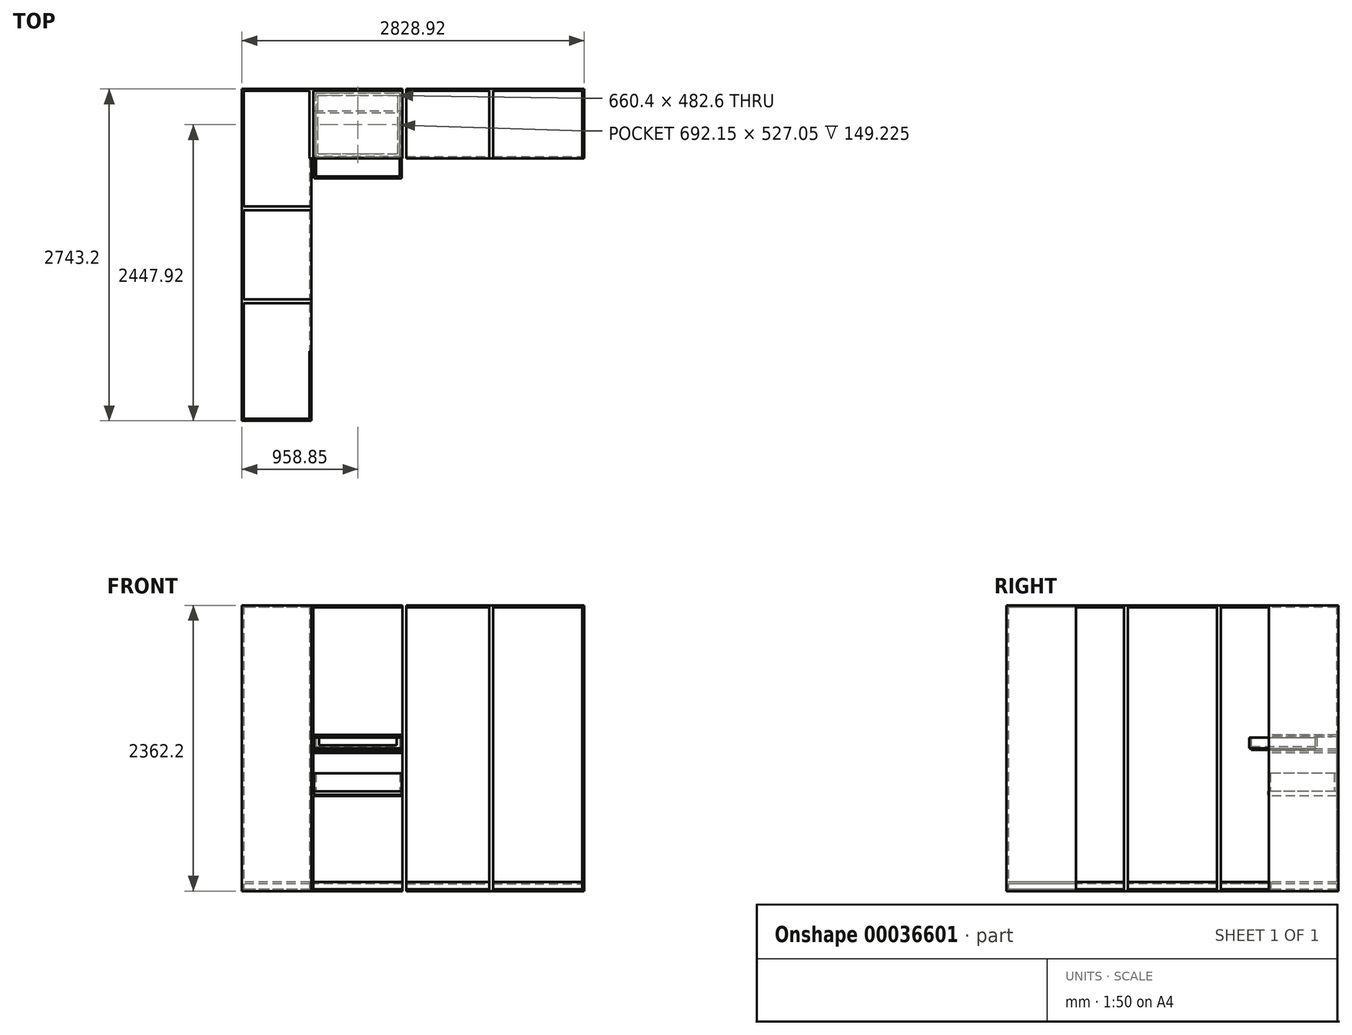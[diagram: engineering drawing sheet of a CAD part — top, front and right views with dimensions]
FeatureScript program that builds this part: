
annotation { "Feature Type Name" : "Feature", "Feature Type Description" : "" }
export const myFeature = defineFeature(function(context is Context, id is Id, definition is map)
    precondition{}
    {
        {
            var Q0;
            Q0=qCreatedBy(makeId("Top.planeOp"),FACE);
            var sketch = newSketch(context, id + "F0", { "sketchPlane" : qUnion([Q0])});
            skLineSegment(sketch, "E0.rect.bottom", {"start": v(384.18, 287.34) * mm, "end": v(-384.18, 287.34) * mm});
            skLineSegment(sketch, "E0.rect.top", {"start": v(384.18, -287.34) * mm, "end": v(-384.18, -287.34) * mm});
            skLineSegment(sketch, "E0.rect.left", {"start": v(384.18, 287.34) * mm, "end": v(384.18, -287.34) * mm});
            skLineSegment(sketch, "E0.rect.right", {"start": v(-384.18, 287.34) * mm, "end": v(-384.18, -287.34) * mm});
            skPoint(sketch, "E0.rect.middle", {"position": v(0, 0) * mm});
            skLineSegment(sketch, "E1.bottom", {"start": v(384.18, -287.34) * mm, "end": v(1101.73, -287.34) * mm});
            skLineSegment(sketch, "E1.top", {"start": v(384.17, 287.34) * mm, "end": v(1101.73, 287.34) * mm});
            skLineSegment(sketch, "E1.left", {"start": v(384.18, -287.34) * mm, "end": v(384.18, 287.34) * mm});
            skLineSegment(sketch, "E1.right", {"start": v(1101.73, -287.34) * mm, "end": v(1101.73, 287.34) * mm});
            skLineSegment(sketch, "E2.bottom", {"start": v(1101.73, -287.34) * mm, "end": v(1870.08, -287.34) * mm});
            skLineSegment(sketch, "E2.top", {"start": v(1101.73, 287.34) * mm, "end": v(1870.08, 287.34) * mm});
            skLineSegment(sketch, "E2.right", {"start": v(1870.08, -287.34) * mm, "end": v(1870.08, 287.34) * mm});
            skLineSegment(sketch, "E3.bottom", {"start": v(-384.18, 287.34) * mm, "end": v(-958.85, 287.34) * mm});
            skLineSegment(sketch, "E3.top", {"start": v(-384.17, -2455.86) * mm, "end": v(-958.85, -2455.86) * mm});
            skLineSegment(sketch, "E3.left", {"start": v(-384.18, 287.34) * mm, "end": v(-384.18, -2455.86) * mm});
            skLineSegment(sketch, "E3.right", {"start": v(-958.85, 287.34) * mm, "end": v(-958.85, -2455.86) * mm});
            skLineSegment(sketch, "E4.bottom", {"start": v(-384.17, -2455.86) * mm, "end": v(384.18, -2455.86) * mm});
            skLineSegment(sketch, "E4.top", {"start": v(-384.17, -1881.19) * mm, "end": v(384.18, -1881.19) * mm});
            skLineSegment(sketch, "E4.left", {"start": v(-384.17, -2455.86) * mm, "end": v(-384.17, -1881.19) * mm});
            skLineSegment(sketch, "E4.right", {"start": v(384.18, -2455.86) * mm, "end": v(384.18, -1881.19) * mm});
            skLineSegment(sketch, "E5.bottom", {"start": v(384.18, -2455.86) * mm, "end": v(1101.73, -2455.86) * mm});
            skLineSegment(sketch, "E5.top", {"start": v(384.18, -1881.19) * mm, "end": v(1101.73, -1881.19) * mm});
            skLineSegment(sketch, "E5.right", {"start": v(1101.73, -2455.86) * mm, "end": v(1101.73, -1881.19) * mm});
            skLineSegment(sketch, "E6.bottom", {"start": v(1101.73, -2455.86) * mm, "end": v(1870.08, -2455.86) * mm});
            skLineSegment(sketch, "E6.top", {"start": v(1101.73, -1881.19) * mm, "end": v(1870.08, -1881.19) * mm});
            skLineSegment(sketch, "E6.right", {"start": v(1870.08, -2455.86) * mm, "end": v(1870.08, -1881.19) * mm});
            skLineSegment(sketch, "E7.0", {"start": v(1117.6, -271.46) * mm, "end": v(1117.6, 271.46) * mm});
            skLineSegment(sketch, "E7.1", {"start": v(1117.6, -271.46) * mm, "end": v(1854.2, -271.46) * mm});
            skLineSegment(sketch, "E7.2", {"start": v(1854.2, -271.46) * mm, "end": v(1854.2, 271.46) * mm});
            skLineSegment(sketch, "E7.3", {"start": v(1117.6, 271.46) * mm, "end": v(1854.2, 271.46) * mm});
            skLineSegment(sketch, "E8", {"start": v(1117.6, -271.46) * mm, "end": v(1117.6, -287.34) * mm});
            skLineSegment(sketch, "E9", {"start": v(1117.6, 271.46) * mm, "end": v(1117.6, 287.34) * mm});
            skLineSegment(sketch, "E10", {"start": v(1854.2, 271.46) * mm, "end": v(1854.2, 287.34) * mm});
            skLineSegment(sketch, "E11", {"start": v(1854.2, -271.46) * mm, "end": v(1854.2, -287.34) * mm});
            skLineSegment(sketch, "E12.0", {"start": v(400.05, 271.46) * mm, "end": v(1085.85, 271.46) * mm});
            skLineSegment(sketch, "E12.1", {"start": v(400.05, -271.46) * mm, "end": v(400.05, 271.46) * mm});
            skLineSegment(sketch, "E12.2", {"start": v(400.05, -271.46) * mm, "end": v(1085.85, -271.46) * mm});
            skLineSegment(sketch, "E12.3", {"start": v(1085.85, -271.46) * mm, "end": v(1085.85, 271.46) * mm});
            skLineSegment(sketch, "E13", {"start": v(400.05, 271.46) * mm, "end": v(400.05, 287.34) * mm});
            skLineSegment(sketch, "E14", {"start": v(400.05, -271.46) * mm, "end": v(400.05, -287.34) * mm});
            skLineSegment(sketch, "E15", {"start": v(1085.85, -271.46) * mm, "end": v(1085.85, -287.34) * mm});
            skLineSegment(sketch, "E16", {"start": v(1085.85, 271.46) * mm, "end": v(1085.85, 287.34) * mm});
            skLineSegment(sketch, "E17.0", {"start": v(368.3, -271.46) * mm, "end": v(-368.3, -271.46) * mm});
            skLineSegment(sketch, "E17.1", {"start": v(368.3, -271.46) * mm, "end": v(368.3, 271.46) * mm});
            skLineSegment(sketch, "E17.2", {"start": v(368.3, 271.46) * mm, "end": v(-368.3, 271.46) * mm});
            skLineSegment(sketch, "E17.3", {"start": v(-368.3, 271.46) * mm, "end": v(-368.3, -271.46) * mm});
            skLineSegment(sketch, "E18", {"start": v(-368.3, -271.46) * mm, "end": v(-368.3, -287.34) * mm});
            skLineSegment(sketch, "E19", {"start": v(-368.3, 271.46) * mm, "end": v(-368.3, 287.34) * mm});
            skLineSegment(sketch, "E20", {"start": v(368.3, 271.46) * mm, "end": v(368.3, 287.34) * mm});
            skLineSegment(sketch, "E21", {"start": v(368.3, -271.46) * mm, "end": v(368.3, -287.34) * mm});
            skLineSegment(sketch, "E22.0", {"start": v(-400.05, 271.46) * mm, "end": v(-400.05, -684.21) * mm});
            skLineSegment(sketch, "E22.1", {"start": v(-400.05, 271.46) * mm, "end": v(-942.98, 271.46) * mm});
            skLineSegment(sketch, "E22.2", {"start": v(-942.98, 271.46) * mm, "end": v(-942.97, -684.21) * mm});
            skLineSegment(sketch, "E22.3", {"start": v(-400.05, -2439.99) * mm, "end": v(-942.97, -2439.99) * mm});
            skLineSegment(sketch, "E23.0", {"start": v(-368.3, -2439.99) * mm, "end": v(368.3, -2439.99) * mm});
            skLineSegment(sketch, "E23.1", {"start": v(-368.3, -2439.99) * mm, "end": v(-368.3, -1897.06) * mm});
            skLineSegment(sketch, "E23.2", {"start": v(-368.3, -1897.06) * mm, "end": v(368.3, -1897.06) * mm});
            skLineSegment(sketch, "E23.3", {"start": v(368.3, -2439.99) * mm, "end": v(368.3, -1897.06) * mm});
            skLineSegment(sketch, "E24.0", {"start": v(400.05, -2439.99) * mm, "end": v(1085.85, -2439.99) * mm});
            skLineSegment(sketch, "E24.1", {"start": v(400.05, -2439.99) * mm, "end": v(400.05, -1897.06) * mm});
            skLineSegment(sketch, "E24.2", {"start": v(400.05, -1897.06) * mm, "end": v(1085.85, -1897.06) * mm});
            skLineSegment(sketch, "E24.3", {"start": v(1085.85, -2439.99) * mm, "end": v(1085.85, -1897.06) * mm});
            skLineSegment(sketch, "E25.0", {"start": v(1117.6, -2439.99) * mm, "end": v(1117.6, -1897.06) * mm});
            skLineSegment(sketch, "E25.1", {"start": v(1117.6, -2439.99) * mm, "end": v(1854.2, -2439.99) * mm});
            skLineSegment(sketch, "E25.2", {"start": v(1854.2, -2439.99) * mm, "end": v(1854.2, -1897.06) * mm});
            skLineSegment(sketch, "E25.3", {"start": v(1117.6, -1897.06) * mm, "end": v(1854.2, -1897.06) * mm});
            skLineSegment(sketch, "E26", {"start": v(-400.05, -2439.99) * mm, "end": v(-384.18, -2439.99) * mm});
            skLineSegment(sketch, "E27", {"start": v(-942.97, -2439.99) * mm, "end": v(-958.85, -2439.99) * mm});
            skLineSegment(sketch, "E28", {"start": v(-400.05, 271.46) * mm, "end": v(-384.18, 271.46) * mm});
            skLineSegment(sketch, "E29", {"start": v(-942.98, 271.46) * mm, "end": v(-958.85, 271.46) * mm});
            skLineSegment(sketch, "E30", {"start": v(-368.3, -1897.06) * mm, "end": v(-368.3, -1881.19) * mm});
            skLineSegment(sketch, "E31", {"start": v(368.3, -1897.06) * mm, "end": v(368.3, -1881.19) * mm});
            skLineSegment(sketch, "E32", {"start": v(400.05, -1897.06) * mm, "end": v(400.05, -1881.19) * mm});
            skLineSegment(sketch, "E33", {"start": v(-368.3, -2439.99) * mm, "end": v(-368.3, -2455.86) * mm});
            skLineSegment(sketch, "E34", {"start": v(368.3, -2439.99) * mm, "end": v(368.3, -2455.86) * mm});
            skLineSegment(sketch, "E35", {"start": v(400.05, -2439.99) * mm, "end": v(400.05, -2455.86) * mm});
            skLineSegment(sketch, "E36", {"start": v(1117.6, -2439.99) * mm, "end": v(1117.6, -2455.86) * mm});
            skLineSegment(sketch, "E37", {"start": v(1085.85, -2439.99) * mm, "end": v(1085.85, -2455.86) * mm});
            skLineSegment(sketch, "E38", {"start": v(1085.85, -1897.06) * mm, "end": v(1085.85, -1881.19) * mm});
            skLineSegment(sketch, "E39", {"start": v(1117.6, -1897.06) * mm, "end": v(1117.6, -1881.19) * mm});
            skLineSegment(sketch, "E40", {"start": v(1854.2, -2439.99) * mm, "end": v(1854.2, -2455.86) * mm});
            skLineSegment(sketch, "E41", {"start": v(1854.2, -1897.06) * mm, "end": v(1854.2, -1881.19) * mm});
            skLineSegment(sketch, "E42.0", {"start": v(-384.17, -700.09) * mm, "end": v(-958.85, -700.09) * mm});
            skLineSegment(sketch, "E43.0", {"start": v(-384.17, -1468.44) * mm, "end": v(-958.85, -1468.44) * mm});
            skLineSegment(sketch, "E44.0", {"start": v(-384.17, -1452.56) * mm, "end": v(-958.85, -1452.56) * mm});
            skLineSegment(sketch, "E45.0", {"start": v(-384.17, -684.21) * mm, "end": v(-958.85, -684.21) * mm});
            skLineSegment(sketch, "E46.0", {"start": v(-384.17, -715.96) * mm, "end": v(-958.85, -715.96) * mm});
            skLineSegment(sketch, "E47.0", {"start": v(-384.17, -1484.31) * mm, "end": v(-958.85, -1484.31) * mm});
            skLineSegment(sketch, "E48.trimOffspring", {"start": v(-400.05, -715.96) * mm, "end": v(-400.05, -1452.56) * mm});
            skLineSegment(sketch, "E49.trimOffspring", {"start": v(-942.97, -715.96) * mm, "end": v(-942.97, -1452.56) * mm});
            skLineSegment(sketch, "E50.trimOffspring", {"start": v(-400.05, -1484.31) * mm, "end": v(-400.05, -2439.99) * mm});
            skLineSegment(sketch, "E51.trimOffspring", {"start": v(-942.97, -1484.31) * mm, "end": v(-942.97, -2439.99) * mm});
            skLineSegment(sketch, "E52", {"start": v(-384.18, -287.34) * mm, "end": v(-400.05, -287.34) * mm});
            skLineSegment(sketch, "E53", {"start": v(-384.17, -1881.19) * mm, "end": v(-400.05, -1881.19) * mm});
            skSolve(sketch);
        }
        {
            var Q0;
            {var subQ2=sQuery(id+"F0.wireOp",EDGE,"E2.right");Q0=makeQuery(id+"F0.imprint","IMPRINT",FACE,{"disambiguationData":[TD([[makeQuery(id+"F0.imprint","IMPRINT",EDGE,{"derivedFrom":subQ2}),1.0]])]});}
            var Q1;
            Q1=makeQuery(id+"F0.imprint","IMPRINT",FACE,{"disambiguationData":[TD([[makeQuery(id+"F0.imprint","IMPRINT",EDGE,{"derivedFrom":sQuery(id+"F0.wireOp",EDGE,"E7.3")}),1.0]])]});
            var Q2;
            Q2=makeQuery(id+"F0.imprint","IMPRINT",FACE,{"disambiguationData":[TD([[makeQuery(id+"F0.imprint","IMPRINT",EDGE,{"derivedFrom":sQuery(id+"F0.wireOp",EDGE,"E12.0")}),1.0]])]});
            var Q3;
            {var subQ2=sQuery(id+"F0.wireOp",EDGE,"E1.right");Q3=makeQuery(id+"F0.imprint","IMPRINT",FACE,{"disambiguationData":[TD([[makeQuery(id+"F0.imprint","IMPRINT",EDGE,{"derivedFrom":subQ2}),1.0]])]});}
            var Q4;
            {var subQ2=sQuery(id+"F0.wireOp",EDGE,"E1.right");Q4=makeQuery(id+"F0.imprint","IMPRINT",FACE,{"disambiguationData":[TD([[makeQuery(id+"F0.imprint","IMPRINT",EDGE,{"derivedFrom":subQ2}),-1.0]])]});}
            var Q5;
            Q5=makeQuery(id+"F0.imprint","IMPRINT",FACE,{"disambiguationData":[TD([[makeQuery(id+"F0.imprint","IMPRINT",EDGE,{"derivedFrom":sQuery(id+"F0.wireOp",EDGE,"E17.2")}),-1.0]])]});
            var Q6;
            Q6=makeQuery(id+"F0.imprint","IMPRINT",FACE,{"disambiguationData":[TD([[makeQuery(id+"F0.imprint","IMPRINT",EDGE,{"derivedFrom":sQuery(id+"F0.wireOp",EDGE,"E17.3")}),-1.0]])]});
            var Q7;
            {var subQ1=sQuery(id+"F0.wireOp",EDGE,"E28");Q7=makeQuery(id+"F0.imprint","IMPRINT",FACE,{"disambiguationData":[TD([[makeQuery(id+"F0.imprint","IMPRINT",EDGE,{"derivedFrom":subQ1}),-1.0]])]});}
            var Q8;
            {var subQ3=sQuery(id+"F0.wireOp",EDGE,"E3.bottom");Q8=makeQuery(id+"F0.imprint","IMPRINT",FACE,{"disambiguationData":[TD([[makeQuery(id+"F0.imprint","IMPRINT",EDGE,{"derivedFrom":subQ3}),1.0]])]});}
            var Q9;
            {var subQ3=sQuery(id+"F0.wireOp",EDGE,"E22.2");Q9=makeQuery(id+"F0.imprint","IMPRINT",FACE,{"disambiguationData":[TD([[makeQuery(id+"F0.imprint","IMPRINT",EDGE,{"derivedFrom":subQ3}),-1.0]])]});}
            var Q10;
            {var subQ7=sQuery(id+"F0.wireOp",EDGE,"E42.0");Q10=makeQuery(id+"F0.imprint","IMPRINT",FACE,{"disambiguationData":[TD([[makeQuery(id+"F0.imprint","IMPRINT",EDGE,{"derivedFrom":subQ7}),-1.0]])]});}
            var Q11;
            {var subQ7=sQuery(id+"F0.wireOp",EDGE,"E42.0");Q11=makeQuery(id+"F0.imprint","IMPRINT",FACE,{"disambiguationData":[TD([[makeQuery(id+"F0.imprint","IMPRINT",EDGE,{"derivedFrom":subQ7}),1.0]])]});}
            var Q12;
            {var subQ1=sQuery(id+"F0.wireOp",EDGE,"E49.trimOffspring");Q12=makeQuery(id+"F0.imprint","IMPRINT",FACE,{"disambiguationData":[TD([[makeQuery(id+"F0.imprint","IMPRINT",EDGE,{"derivedFrom":subQ1}),-1.0]])]});}
            var Q13;
            {var subQ4=sQuery(id+"F0.wireOp",EDGE,"E27");Q13=makeQuery(id+"F0.imprint","IMPRINT",FACE,{"disambiguationData":[TD([[makeQuery(id+"F0.imprint","IMPRINT",EDGE,{"derivedFrom":subQ4}),-1.0]])]});}
            var Q14;
            {var subQ7=sQuery(id+"F0.wireOp",EDGE,"E43.0");Q14=makeQuery(id+"F0.imprint","IMPRINT",FACE,{"disambiguationData":[TD([[makeQuery(id+"F0.imprint","IMPRINT",EDGE,{"derivedFrom":subQ7}),1.0]])]});}
            var Q15;
            {var subQ7=sQuery(id+"F0.wireOp",EDGE,"E43.0");Q15=makeQuery(id+"F0.imprint","IMPRINT",FACE,{"disambiguationData":[TD([[makeQuery(id+"F0.imprint","IMPRINT",EDGE,{"derivedFrom":subQ7}),-1.0]])]});}
            var Q16;
            {var subQ3=sQuery(id+"F0.wireOp",EDGE,"E3.top");Q16=makeQuery(id+"F0.imprint","IMPRINT",FACE,{"disambiguationData":[TD([[makeQuery(id+"F0.imprint","IMPRINT",EDGE,{"derivedFrom":subQ3}),-1.0]])]});}
            var Q17;
            {var subQ2=sQuery(id+"F0.wireOp",EDGE,"E26");Q17=makeQuery(id+"F0.imprint","IMPRINT",FACE,{"disambiguationData":[TD([[makeQuery(id+"F0.imprint","IMPRINT",EDGE,{"derivedFrom":subQ2}),1.0]])]});}
            var Q18;
            {var subQ2=sQuery(id+"F0.wireOp",EDGE,"E1.left");Q18=makeQuery(id+"F0.imprint","IMPRINT",FACE,{"disambiguationData":[TD([[makeQuery(id+"F0.imprint","IMPRINT",EDGE,{"derivedFrom":subQ2}),1.0]])]});}
            var Q19;
            {var subQ2=sQuery(id+"F0.wireOp",EDGE,"E1.left");Q19=makeQuery(id+"F0.imprint","IMPRINT",FACE,{"disambiguationData":[TD([[makeQuery(id+"F0.imprint","IMPRINT",EDGE,{"derivedFrom":subQ2}),-1.0]])]});}
            extrude(context, id + "F1", {"entities" : qUnion([Q0, Q1, Q2, Q3, Q4, Q5, Q6, Q7, Q8, Q9, Q10, Q11, Q12, Q13, Q14, Q15, Q16, Q17, Q18, Q19]), "depth" : 2362.2 * mm});
        }
        {
            var Q0;
            {var subQ1=sQuery(id+"F0.wireOp",EDGE,"E48.trimOffspring");Q0=makeQuery(id+"F0.imprint","IMPRINT",FACE,{"disambiguationData":[TD([[makeQuery(id+"F0.imprint","IMPRINT",EDGE,{"derivedFrom":subQ1}),-1.0]])]});}
            var Q1;
            {var subQ3=sQuery(id+"F0.wireOp",EDGE,"E22.3");Q1=makeQuery(id+"F0.imprint","IMPRINT",FACE,{"disambiguationData":[TD([[makeQuery(id+"F0.imprint","IMPRINT",EDGE,{"derivedFrom":subQ3}),-1.0]])]});}
            var Q2;
            {var subQ0=sQuery(id+"F0.wireOp",EDGE,"E53");Q2=makeQuery(id+"F0.imprint","IMPRINT",FACE,{"disambiguationData":[TD([[makeQuery(id+"F0.imprint","IMPRINT",EDGE,{"derivedFrom":subQ0}),-1.0]])]});}
            var Q3;
            {var subQ1=sQuery(id+"F0.wireOp",EDGE,"E48.trimOffspring");Q3=makeQuery(id+"F0.imprint","IMPRINT",FACE,{"disambiguationData":[TD([[makeQuery(id+"F0.imprint","IMPRINT",EDGE,{"derivedFrom":subQ1}),1.0]])]});}
            var Q4;
            {var subQ0=sQuery(id+"F0.wireOp",EDGE,"E52");Q4=makeQuery(id+"F0.imprint","IMPRINT",FACE,{"disambiguationData":[TD([[makeQuery(id+"F0.imprint","IMPRINT",EDGE,{"derivedFrom":subQ0}),1.0]])]});}
            var Q5;
            Q5=makeQuery(id+"F0.imprint","IMPRINT",FACE,{"disambiguationData":[TD([[makeQuery(id+"F0.imprint","IMPRINT",EDGE,{"derivedFrom":sQuery(id+"F0.wireOp",EDGE,"E17.0")}),1.0]])]});
            var Q6;
            Q6=makeQuery(id+"F0.imprint","IMPRINT",FACE,{"disambiguationData":[TD([[makeQuery(id+"F0.imprint","IMPRINT",EDGE,{"derivedFrom":sQuery(id+"F0.wireOp",EDGE,"E7.1")}),-1.0]])]});
            var Q7;
            Q7=makeQuery(id+"F0.imprint","IMPRINT",FACE,{"disambiguationData":[TD([[makeQuery(id+"F0.imprint","IMPRINT",EDGE,{"derivedFrom":sQuery(id+"F0.wireOp",EDGE,"E12.2")}),-1.0]])]});
            var Q8;
            {var subQ4=sQuery(id+"F0.wireOp",EDGE,"E22.1");Q8=makeQuery(id+"F0.imprint","IMPRINT",FACE,{"disambiguationData":[TD([[makeQuery(id+"F0.imprint","IMPRINT",EDGE,{"derivedFrom":subQ4}),1.0]])]});}
            var Q9;
            Q9=makeQuery(id+"F0.imprint","IMPRINT",FACE,{"disambiguationData":[TD([[makeQuery(id+"F0.imprint","IMPRINT",EDGE,{"derivedFrom":sQuery(id+"F0.wireOp",EDGE,"E17.0")}),-1.0]])]});
            var Q10;
            Q10=makeQuery(id+"F0.imprint","IMPRINT",FACE,{"disambiguationData":[TD([[makeQuery(id+"F0.imprint","IMPRINT",EDGE,{"derivedFrom":sQuery(id+"F0.wireOp",EDGE,"E12.0")}),-1.0]])]});
            var Q11;
            Q11=makeQuery(id+"F0.imprint","IMPRINT",FACE,{"disambiguationData":[TD([[makeQuery(id+"F0.imprint","IMPRINT",EDGE,{"derivedFrom":sQuery(id+"F0.wireOp",EDGE,"E7.0")}),-1.0]])]});
            extrude(context, id + "F2", {"entities" : qUnion([Q0, Q1, Q2, Q3, Q4, Q5, Q6, Q7, Q8, Q9, Q10, Q11]), "depth" : 15.88 * mm});
        }
        {
            var Q0;
            Q0=makeQuery(id+"F0.imprint","IMPRINT",FACE,{"disambiguationData":[TD([[makeQuery(id+"F0.imprint","IMPRINT",EDGE,{"derivedFrom":sQuery(id+"F0.wireOp",EDGE,"E12.2")}),-1.0]])]});
            var Q1;
            Q1=makeQuery(id+"F0.imprint","IMPRINT",FACE,{"disambiguationData":[TD([[makeQuery(id+"F0.imprint","IMPRINT",EDGE,{"derivedFrom":sQuery(id+"F0.wireOp",EDGE,"E7.1")}),-1.0]])]});
            var Q2;
            Q2=makeQuery(id+"F0.imprint","IMPRINT",FACE,{"disambiguationData":[TD([[makeQuery(id+"F0.imprint","IMPRINT",EDGE,{"derivedFrom":sQuery(id+"F0.wireOp",EDGE,"E7.0")}),-1.0]])]});
            var Q3;
            Q3=makeQuery(id+"F0.imprint","IMPRINT",FACE,{"disambiguationData":[TD([[makeQuery(id+"F0.imprint","IMPRINT",EDGE,{"derivedFrom":sQuery(id+"F0.wireOp",EDGE,"E12.0")}),-1.0]])]});
            var Q4;
            Q4=makeQuery(id+"F0.imprint","IMPRINT",FACE,{"disambiguationData":[TD([[makeQuery(id+"F0.imprint","IMPRINT",EDGE,{"derivedFrom":sQuery(id+"F0.wireOp",EDGE,"E17.0")}),-1.0]])]});
            var Q5;
            {var subQ4=sQuery(id+"F0.wireOp",EDGE,"E22.1");Q5=makeQuery(id+"F0.imprint","IMPRINT",FACE,{"disambiguationData":[TD([[makeQuery(id+"F0.imprint","IMPRINT",EDGE,{"derivedFrom":subQ4}),1.0]])]});}
            var Q6;
            Q6=makeQuery(id+"F0.imprint","IMPRINT",FACE,{"disambiguationData":[TD([[makeQuery(id+"F0.imprint","IMPRINT",EDGE,{"derivedFrom":sQuery(id+"F0.wireOp",EDGE,"E17.0")}),1.0]])]});
            var Q7;
            {var subQ0=sQuery(id+"F0.wireOp",EDGE,"E52");Q7=makeQuery(id+"F0.imprint","IMPRINT",FACE,{"disambiguationData":[TD([[makeQuery(id+"F0.imprint","IMPRINT",EDGE,{"derivedFrom":subQ0}),1.0]])]});}
            var Q8;
            {var subQ1=sQuery(id+"F0.wireOp",EDGE,"E48.trimOffspring");Q8=makeQuery(id+"F0.imprint","IMPRINT",FACE,{"disambiguationData":[TD([[makeQuery(id+"F0.imprint","IMPRINT",EDGE,{"derivedFrom":subQ1}),-1.0]])]});}
            var Q9;
            {var subQ1=sQuery(id+"F0.wireOp",EDGE,"E48.trimOffspring");Q9=makeQuery(id+"F0.imprint","IMPRINT",FACE,{"disambiguationData":[TD([[makeQuery(id+"F0.imprint","IMPRINT",EDGE,{"derivedFrom":subQ1}),1.0]])]});}
            var Q10;
            {var subQ0=sQuery(id+"F0.wireOp",EDGE,"E53");Q10=makeQuery(id+"F0.imprint","IMPRINT",FACE,{"disambiguationData":[TD([[makeQuery(id+"F0.imprint","IMPRINT",EDGE,{"derivedFrom":subQ0}),-1.0]])]});}
            var Q11;
            {var subQ3=sQuery(id+"F0.wireOp",EDGE,"E22.3");Q11=makeQuery(id+"F0.imprint","IMPRINT",FACE,{"disambiguationData":[TD([[makeQuery(id+"F0.imprint","IMPRINT",EDGE,{"derivedFrom":subQ3}),-1.0]])]});}
            extrude(context, id + "F3", {"entities" : qUnion([Q0, Q1, Q2, Q3, Q4, Q5, Q6, Q7, Q8, Q9, Q10, Q11]), "depth" : 2362.2 * mm, "hasSecondDirection" : true, "secondDirectionOppositeDirection" : false, "secondDirectionDepth" : 2346.32 * mm});
        }
        {
            var Q0;
            {var subQ4=sQuery(id+"F0.wireOp",EDGE,"E22.1");Q0=makeQuery(id+"F0.imprint","IMPRINT",FACE,{"disambiguationData":[TD([[makeQuery(id+"F0.imprint","IMPRINT",EDGE,{"derivedFrom":subQ4}),1.0]])]});}
            var Q1;
            {var subQ1=sQuery(id+"F0.wireOp",EDGE,"E48.trimOffspring");Q1=makeQuery(id+"F0.imprint","IMPRINT",FACE,{"disambiguationData":[TD([[makeQuery(id+"F0.imprint","IMPRINT",EDGE,{"derivedFrom":subQ1}),-1.0]])]});}
            var Q2;
            {var subQ3=sQuery(id+"F0.wireOp",EDGE,"E22.3");Q2=makeQuery(id+"F0.imprint","IMPRINT",FACE,{"disambiguationData":[TD([[makeQuery(id+"F0.imprint","IMPRINT",EDGE,{"derivedFrom":subQ3}),-1.0]])]});}
            var Q3;
            Q3=makeQuery(id+"F0.imprint","IMPRINT",FACE,{"disambiguationData":[TD([[makeQuery(id+"F0.imprint","IMPRINT",EDGE,{"derivedFrom":sQuery(id+"F0.wireOp",EDGE,"E17.0")}),-1.0]])]});
            var Q4;
            Q4=makeQuery(id+"F0.imprint","IMPRINT",FACE,{"disambiguationData":[TD([[makeQuery(id+"F0.imprint","IMPRINT",EDGE,{"derivedFrom":sQuery(id+"F0.wireOp",EDGE,"E7.0")}),-1.0]])]});
            var Q5;
            Q5=makeQuery(id+"F0.imprint","IMPRINT",FACE,{"disambiguationData":[TD([[makeQuery(id+"F0.imprint","IMPRINT",EDGE,{"derivedFrom":sQuery(id+"F0.wireOp",EDGE,"E12.0")}),-1.0]])]});
            extrude(context, id + "F4", {"entities" : qUnion([Q0, Q1, Q2, Q3, Q4, Q5]), "operationType" : NewBodyOperationType.ADD, "depth" : 76.2 * mm, "hasSecondDirection" : true, "secondDirectionOppositeDirection" : false, "secondDirectionDepth" : 60.32 * mm});
        }
        {
            var Q0;
            {var subQ0=sQuery(id+"F0.wireOp",EDGE,"E53");Q0=makeQuery(id+"F0.imprint","IMPRINT",FACE,{"disambiguationData":[TD([[makeQuery(id+"F0.imprint","IMPRINT",EDGE,{"derivedFrom":subQ0}),-1.0]])]});}
            var Q1;
            {var subQ1=sQuery(id+"F0.wireOp",EDGE,"E48.trimOffspring");Q1=makeQuery(id+"F0.imprint","IMPRINT",FACE,{"disambiguationData":[TD([[makeQuery(id+"F0.imprint","IMPRINT",EDGE,{"derivedFrom":subQ1}),1.0]])]});}
            var Q2;
            Q2=makeQuery(id+"F0.imprint","IMPRINT",FACE,{"disambiguationData":[TD([[makeQuery(id+"F0.imprint","IMPRINT",EDGE,{"derivedFrom":sQuery(id+"F0.wireOp",EDGE,"E17.0")}),1.0]])]});
            var Q3;
            {var subQ0=sQuery(id+"F0.wireOp",EDGE,"E52");Q3=makeQuery(id+"F0.imprint","IMPRINT",FACE,{"disambiguationData":[TD([[makeQuery(id+"F0.imprint","IMPRINT",EDGE,{"derivedFrom":subQ0}),1.0]])]});}
            var Q4;
            Q4=makeQuery(id+"F0.imprint","IMPRINT",FACE,{"disambiguationData":[TD([[makeQuery(id+"F0.imprint","IMPRINT",EDGE,{"derivedFrom":sQuery(id+"F0.wireOp",EDGE,"E12.2")}),-1.0]])]});
            var Q5;
            Q5=makeQuery(id+"F0.imprint","IMPRINT",FACE,{"disambiguationData":[TD([[makeQuery(id+"F0.imprint","IMPRINT",EDGE,{"derivedFrom":sQuery(id+"F0.wireOp",EDGE,"E7.1")}),-1.0]])]});
            extrude(context, id + "F5", {"entities" : qUnion([Q0, Q1, Q2, Q3, Q4, Q5]), "depth" : 76.2 * mm});
        }
        {
            var Q0;
            Q0=makeQuery(id+"F0.imprint","IMPRINT",FACE,{"disambiguationData":[TD([[makeQuery(id+"F0.imprint","IMPRINT",EDGE,{"derivedFrom":sQuery(id+"F0.wireOp",EDGE,"E17.0")}),-1.0]])]});
            var Q1;
            Q1=makeQuery(id+"F0.imprint","IMPRINT",FACE,{"disambiguationData":[TD([[makeQuery(id+"F0.imprint","IMPRINT",EDGE,{"derivedFrom":sQuery(id+"F0.wireOp",EDGE,"E17.0")}),1.0]])]});
            extrude(context, id + "F6", {"entities" : qUnion([Q0, Q1]), "depth" : 803.27 * mm, "hasSecondDirection" : true, "secondDirectionOppositeDirection" : false, "secondDirectionDepth" : 787.4 * mm});
        }
        {
            var Q0;
            Q0=makeQuery(id+"F6.opExtrude","SWEPT_BODY",BODY,{"disambiguationData":[OSD([sQuery(id+"F0.wireOp",EDGE,"E0.rect.top"),sQuery(id+"F0.wireOp",EDGE,"E17.1"),sQuery(id+"F0.wireOp",EDGE,"E17.2"),sQuery(id+"F0.wireOp",EDGE,"E17.3"),sQuery(id+"F0.wireOp",EDGE,"E18"),sQuery(id+"F0.wireOp",EDGE,"E21")])]});
            transform(context, id + "F7", {"entities" : qUnion([Q0]), "transformType" : TransformType.TRANSLATION_3D, "dx" : 0 * mm, "dy" : 0 * mm, "dz" : 355.6 * mm, "makeCopy" : true});
        }
        {
            var Q0;
            Q0=makeQuery(id+"F7.opPattern","COPY",BODY,{"derivedFrom":makeQuery(id+"F6.opExtrude","SWEPT_BODY",BODY,{"disambiguationData":[OSD([sQuery(id+"F0.wireOp",EDGE,"E0.rect.top"),sQuery(id+"F0.wireOp",EDGE,"E17.1"),sQuery(id+"F0.wireOp",EDGE,"E17.2"),sQuery(id+"F0.wireOp",EDGE,"E17.3"),sQuery(id+"F0.wireOp",EDGE,"E18"),sQuery(id+"F0.wireOp",EDGE,"E21")])]}),"instanceName":"1"});
            transform(context, id + "F8", {"entities" : qUnion([Q0]), "transformType" : TransformType.TRANSLATION_3D, "dx" : 0 * mm, "dy" : 0 * mm, "dz" : 15.88 * mm, "makeCopy" : true});
        }
        {
            var Q0;
            Q0=makeQuery(id+"F8.opPattern","COPY",FACE,{"derivedFrom":makeQuery(id+"F7.opPattern","COPY",FACE,{"derivedFrom":makeQuery(id+"F6.opExtrude","CAP_FACE",FACE,{"disambiguationData":[OSD([sQuery(id+"F0.wireOp",EDGE,"E0.rect.top"),sQuery(id+"F0.wireOp",EDGE,"E17.1"),sQuery(id+"F0.wireOp",EDGE,"E17.2"),sQuery(id+"F0.wireOp",EDGE,"E17.3"),sQuery(id+"F0.wireOp",EDGE,"E18"),sQuery(id+"F0.wireOp",EDGE,"E21")])],"isStart":false}),"instanceName":"1"}),"instanceName":"1"});
            var sketch = newSketch(context, id + "F9", { "sketchPlane" : qUnion([Q0])});
            skLineSegment(sketch, "E54", {"start": v(-361.95, -451.32) * mm, "end": v(361.95, -451.32) * mm});
            skPoint(sketch, "E55.orphan", {"position": v(361.95, -961.87) * mm});
            skLineSegment(sketch, "E56.0", {"start": v(-361.95, 107.48) * mm, "end": v(361.95, 107.48) * mm});
            skLineSegment(sketch, "E57", {"start": v(-361.95, -451.32) * mm, "end": v(-361.95, 107.48) * mm});
            skLineSegment(sketch, "E58", {"start": v(361.95, -451.32) * mm, "end": v(361.95, 107.48) * mm});
            skLineSegment(sketch, "E59.0", {"start": v(-346.08, 91.6) * mm, "end": v(346.07, 91.6) * mm});
            skLineSegment(sketch, "E60.0", {"start": v(346.08, -435.44) * mm, "end": v(346.08, 91.6) * mm});
            skLineSegment(sketch, "E61.0", {"start": v(-346.08, -435.44) * mm, "end": v(346.07, -435.44) * mm});
            skLineSegment(sketch, "E62.0", {"start": v(-346.08, -435.44) * mm, "end": v(-346.08, 91.6) * mm});
            skLineSegment(sketch, "E63.0", {"start": v(-320.68, -451.32) * mm, "end": v(-320.68, -435.44) * mm});
            skLineSegment(sketch, "E64.0", {"start": v(320.68, -451.32) * mm, "end": v(320.68, -435.44) * mm});
            skSolve(sketch);
        }
        {
            var Q0;
            {var subQ6=sQuery(id+"F9.wireOp",EDGE,"E64.0");Q0=makeQuery(id+"F9.imprint","IMPRINT",FACE,{"disambiguationData":[TD([[makeQuery(id+"F9.imprint","IMPRINT",EDGE,{"derivedFrom":subQ6}),-1.0]])]});}
            var Q1;
            {var subQ10=sQuery(id+"F9.wireOp",EDGE,"E56.0");Q1=makeQuery(id+"F9.imprint","IMPRINT",FACE,{"disambiguationData":[TD([[makeQuery(id+"F9.imprint","IMPRINT",EDGE,{"derivedFrom":subQ10}),-1.0]])]});}
            var Q2;
            {var subQ5=sQuery(id+"F9.wireOp",EDGE,"E63.0");Q2=makeQuery(id+"F9.imprint","IMPRINT",FACE,{"disambiguationData":[TD([[makeQuery(id+"F9.imprint","IMPRINT",EDGE,{"derivedFrom":subQ5}),1.0]])]});}
            extrude(context, id + "F10", {"entities" : qUnion([Q0, Q1, Q2]), "operationType" : NewBodyOperationType.ADD, "depth" : 95.25 * mm, "hasSecondDirection" : true, "secondDirectionOppositeDirection" : false, "secondDirectionDepth" : 6.35 * mm});
        }
        {
            var Q0;
            {var subQ1=sQuery(id+"F9.wireOp",EDGE,"E63.0");Q0=makeQuery(id+"F9.imprint","IMPRINT",FACE,{"disambiguationData":[TD([[makeQuery(id+"F9.imprint","IMPRINT",EDGE,{"derivedFrom":subQ1}),-1.0]])]});}
            extrude(context, id + "F11", {"entities" : qUnion([Q0]), "operationType" : NewBodyOperationType.ADD, "depth" : 31.75 * mm, "hasSecondDirection" : true, "secondDirectionOppositeDirection" : false, "secondDirectionDepth" : 6.35 * mm});
        }
        {
            var Q0;
            {var subQ3=sQuery(id+"F9.wireOp",EDGE,"E60.0");var subQ5=sQuery(id+"F9.wireOp",EDGE,"E61.0");var subQ8=makeQuery(id+"F9.imprint","INTERSECT",VERTEX,{"derivedFrom":[subQ3,subQ5]});Q0=makeQuery(id+"F9.imprint","IMPRINT",FACE,{"disambiguationData":[TD([[makeQuery(id+"F9.imprint","IMPRINT",EDGE,{"disambiguationData":[TD([[subQ8,-1.0]])],"derivedFrom":subQ3}),1.0]])]});}
            var Q1;
            {var subQ3=sQuery(id+"F9.wireOp",EDGE,"E59.0");Q1=makeQuery(id+"F9.imprint","IMPRINT",FACE,{"disambiguationData":[TD([[makeQuery(id+"F9.imprint","IMPRINT",EDGE,{"derivedFrom":subQ3}),-1.0]])]});}
            extrude(context, id + "F12", {"entities" : qUnion([Q0, Q1]), "depth" : 22.22 * mm, "hasSecondDirection" : true, "secondDirectionOppositeDirection" : true, "secondDirectionDepth" : 6.35 * mm});
        }
        {
            var Q0;
            Q0=makeQuery(id+"F11.opExtrude","CAP_FACE",FACE,{"disambiguationData":[OSD([sQuery(id+"F9.wireOp",EDGE,"E54"),sQuery(id+"F9.wireOp",EDGE,"E61.0"),sQuery(id+"F9.wireOp",EDGE,"E63.0"),sQuery(id+"F9.wireOp",EDGE,"E64.0")])],"isStart":false});
            var sketch = newSketch(context, id + "F13", { "sketchPlane" : qUnion([Q0])});
            skLineSegment(sketch, "E65.bottom", {"start": v(-320.68, -451.32) * mm, "end": v(320.68, -451.32) * mm});
            skLineSegment(sketch, "E65.top", {"start": v(-320.68, -435.44) * mm, "end": v(320.68, -435.44) * mm});
            skLineSegment(sketch, "E65.left", {"start": v(-320.68, -451.32) * mm, "end": v(-320.68, -435.44) * mm});
            skLineSegment(sketch, "E65.right", {"start": v(320.68, -451.32) * mm, "end": v(320.68, -435.44) * mm});
            skSolve(sketch);
        }
        {
            var Q0;
            Q0 = qSketchRegion(id + "F13", true);
            extrude(context, id + "F14", {"entities" : qUnion([Q0]), "depth" : 63.5 * mm});
        }
        {
            var Q0;
            Q0=makeQuery(id+"F8.opPattern","COPY",FACE,{"derivedFrom":makeQuery(id+"F7.opPattern","COPY",FACE,{"derivedFrom":makeQuery(id+"F6.opExtrude","CAP_FACE",FACE,{"disambiguationData":[OSD([sQuery(id+"F0.wireOp",EDGE,"E0.rect.top"),sQuery(id+"F0.wireOp",EDGE,"E17.1"),sQuery(id+"F0.wireOp",EDGE,"E17.2"),sQuery(id+"F0.wireOp",EDGE,"E17.3"),sQuery(id+"F0.wireOp",EDGE,"E18"),sQuery(id+"F0.wireOp",EDGE,"E21")])],"isStart":false}),"instanceName":"1"}),"instanceName":"1"});
            var sketch = newSketch(context, id + "F15", { "sketchPlane" : qUnion([Q0])});
            skLineSegment(sketch, "E66.bottom", {"start": v(-368.3, -287.34) * mm, "end": v(368.3, -287.34) * mm});
            skLineSegment(sketch, "E66.top", {"start": v(-368.3, 271.46) * mm, "end": v(368.3, 271.46) * mm});
            skLineSegment(sketch, "E66.left", {"start": v(-368.3, -287.34) * mm, "end": v(-368.3, 271.46) * mm});
            skLineSegment(sketch, "E66.right", {"start": v(368.3, -287.34) * mm, "end": v(368.3, 271.46) * mm});
            skLineSegment(sketch, "E67.0", {"start": v(-330.2, -249.24) * mm, "end": v(330.2, -249.24) * mm});
            skLineSegment(sketch, "E67.1", {"start": v(-330.2, -249.24) * mm, "end": v(-330.2, 233.36) * mm});
            skLineSegment(sketch, "E67.2", {"start": v(-330.2, 233.36) * mm, "end": v(330.2, 233.36) * mm});
            skLineSegment(sketch, "E67.3", {"start": v(330.2, -249.24) * mm, "end": v(330.2, 233.36) * mm});
            skSolve(sketch);
        }
        {
            var Q0;
            Q0=makeQuery(id+"F15.imprint","IMPRINT",FACE,{"disambiguationData":[TD([[makeQuery(id+"F15.imprint","IMPRINT",EDGE,{"derivedFrom":sQuery(id+"F15.wireOp",EDGE,"E66.bottom")}),-1.0]])]});
            extrude(context, id + "F16", {"entities" : qUnion([Q0]), "operationType" : NewBodyOperationType.ADD, "depth" : 117.47 * mm, "hasSecondDirection" : true, "secondDirectionOppositeDirection" : false, "secondDirectionDepth" : 101.6 * mm});
        }
        {
            var Q0;
            Q0=makeQuery(id+"F15.imprint","IMPRINT",FACE,{"disambiguationData":[TD([[makeQuery(id+"F15.imprint","IMPRINT",EDGE,{"derivedFrom":sQuery(id+"F15.wireOp",EDGE,"E67.0")}),1.0]])]});
            var Q1;
            Q1=makeQuery(id+"F8.opPattern","COPY",FACE,{"derivedFrom":makeQuery(id+"F7.opPattern","COPY",FACE,{"derivedFrom":makeQuery(id+"F6.opExtrude","CAP_FACE",FACE,{"disambiguationData":[OSD([sQuery(id+"F0.wireOp",EDGE,"E0.rect.top"),sQuery(id+"F0.wireOp",EDGE,"E17.1"),sQuery(id+"F0.wireOp",EDGE,"E17.2"),sQuery(id+"F0.wireOp",EDGE,"E17.3"),sQuery(id+"F0.wireOp",EDGE,"E18"),sQuery(id+"F0.wireOp",EDGE,"E21")])],"isStart":false}),"instanceName":"1"}),"instanceName":"1"});
            extrude(context, id + "F17", {"entities" : qUnion([Q0, Q1]), "depth" : 117.47 * mm, "hasSecondDirection" : true, "secondDirectionOppositeDirection" : false, "secondDirectionDepth" : 101.6 * mm});
        }
        {
            var Q0;
            Q0=makeQuery(id+"F6.opExtrude","CAP_FACE",FACE,{"disambiguationData":[OSD([sQuery(id+"F0.wireOp",EDGE,"E0.rect.top"),sQuery(id+"F0.wireOp",EDGE,"E17.1"),sQuery(id+"F0.wireOp",EDGE,"E17.2"),sQuery(id+"F0.wireOp",EDGE,"E17.3"),sQuery(id+"F0.wireOp",EDGE,"E18"),sQuery(id+"F0.wireOp",EDGE,"E21")])],"isStart":false});
            var sketch = newSketch(context, id + "F18", { "sketchPlane" : qUnion([Q0])});
            skLineSegment(sketch, "E68", {"start": v(-368.3, -412.28) * mm, "end": v(-361.95, -412.28) * mm});
            skLineSegment(sketch, "E69.trimOffspring", {"start": v(361.95, -412.28) * mm, "end": v(368.3, -412.28) * mm});
            skLineSegment(sketch, "E70.0", {"start": v(-361.95, -290.31) * mm, "end": v(361.95, -290.31) * mm});
            skLineSegment(sketch, "E71.0", {"start": v(-361.95, 268.49) * mm, "end": v(361.95, 268.49) * mm});
            skLineSegment(sketch, "E72", {"start": v(361.95, 268.49) * mm, "end": v(361.95, -290.31) * mm});
            skLineSegment(sketch, "E73", {"start": v(-361.95, -290.31) * mm, "end": v(-361.95, 268.49) * mm});
            skLineSegment(sketch, "E74.0", {"start": v(346.08, 252.61) * mm, "end": v(346.08, -274.44) * mm});
            skLineSegment(sketch, "E75.0", {"start": v(-346.08, -274.44) * mm, "end": v(346.08, -274.44) * mm});
            skLineSegment(sketch, "E76.0", {"start": v(-346.08, -274.44) * mm, "end": v(-346.08, 252.61) * mm});
            skLineSegment(sketch, "E77.0", {"start": v(-346.08, 252.61) * mm, "end": v(346.08, 252.61) * mm});
            skSolve(sketch);
        }
        {
            var Q0;
            {var subQ5=sQuery(id+"F18.wireOp",EDGE,"E71.0");Q0=makeQuery(id+"F18.imprint","IMPRINT",FACE,{"disambiguationData":[TD([[makeQuery(id+"F18.imprint","IMPRINT",EDGE,{"derivedFrom":subQ5}),-1.0]])]});}
            extrude(context, id + "F19", {"entities" : qUnion([Q0]), "depth" : 171.45 * mm, "hasSecondDirection" : true, "secondDirectionOppositeDirection" : false, "secondDirectionDepth" : 6.35 * mm});
        }
        {
            var Q0;
            Q0 = qSketchRegion(id + "F18", true);
            var Q1;
            Q1=makeQuery(id+"F6.opExtrude","CAP_FACE",FACE,{"disambiguationData":[OSD([sQuery(id+"F0.wireOp",EDGE,"E0.rect.top"),sQuery(id+"F0.wireOp",EDGE,"E17.1"),sQuery(id+"F0.wireOp",EDGE,"E17.2"),sQuery(id+"F0.wireOp",EDGE,"E17.3"),sQuery(id+"F0.wireOp",EDGE,"E18"),sQuery(id+"F0.wireOp",EDGE,"E21")])],"isStart":false});
            extrude(context, id + "F20", {"entities" : qUnion([Q0, Q1]), "operationType" : NewBodyOperationType.ADD, "depth" : 22.22 * mm, "hasSecondDirection" : true, "secondDirectionOppositeDirection" : true, "secondDirectionDepth" : 6.35 * mm});
        }
    });
